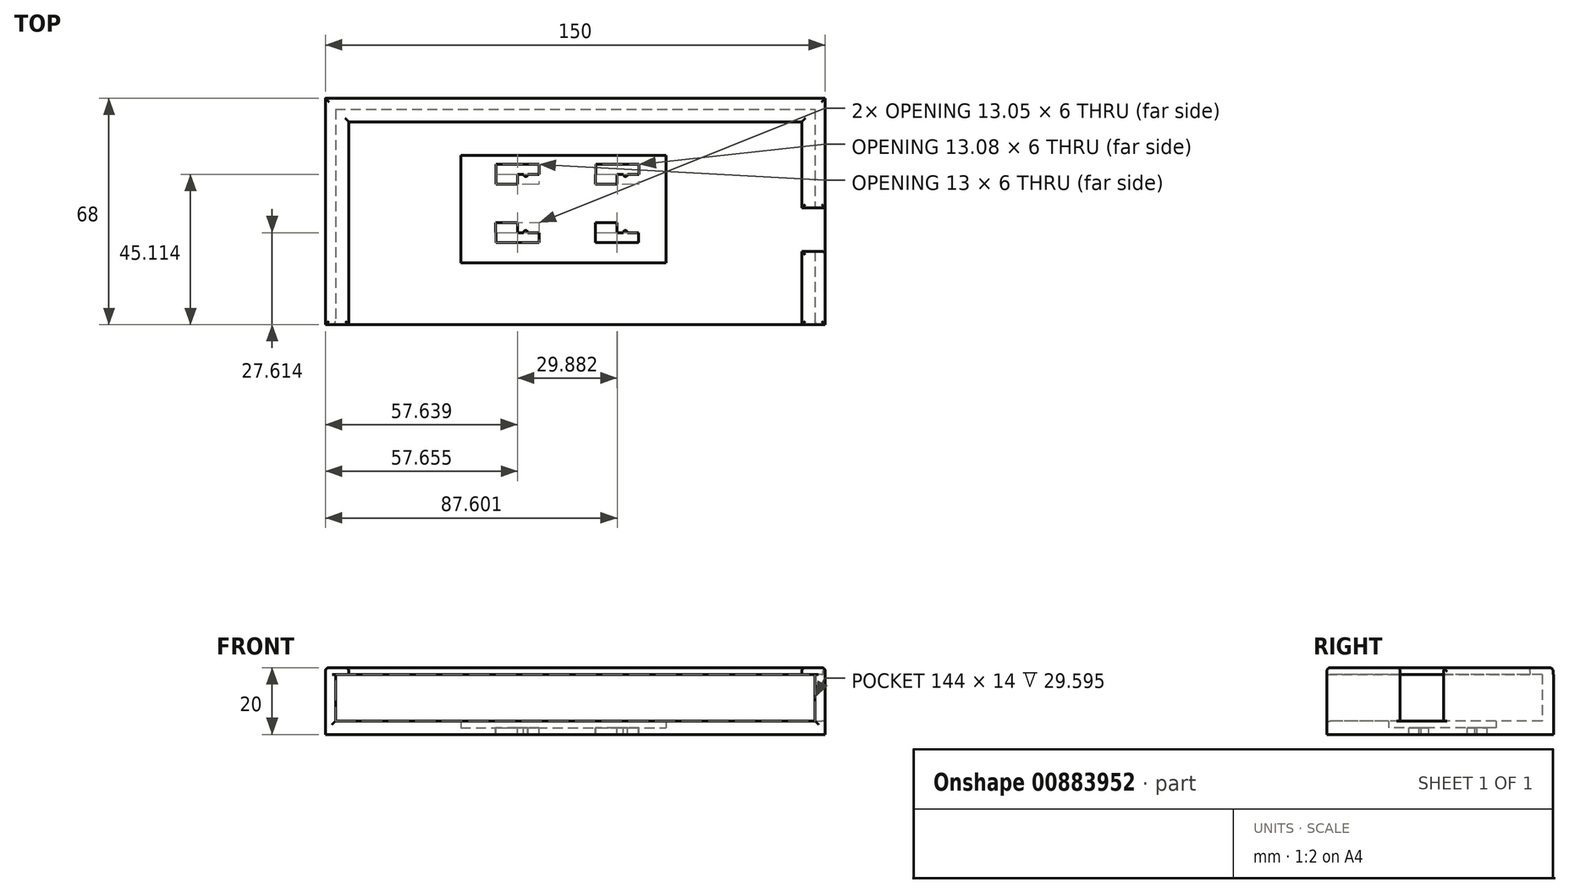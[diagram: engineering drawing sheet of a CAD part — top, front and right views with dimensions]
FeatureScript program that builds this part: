
annotation { "Feature Type Name" : "Feature", "Feature Type Description" : "" }
export const myFeature = defineFeature(function(context is Context, id is Id, definition is map)
    precondition{}
    {
        {
            var Q0;
            Q0=qCreatedBy(makeId("Top.planeOp"),FACE);
            var sketch = newSketch(context, id + "F0", { "sketchPlane" : qUnion([Q0])});
            skLineSegment(sketch, "E0", {"start": v(0, 0) * mm, "end": v(150, 0) * mm});
            skLineSegment(sketch, "E1", {"start": v(150, 0) * mm, "end": v(150, 68) * mm});
            skLineSegment(sketch, "E2", {"start": v(150, 68) * mm, "end": v(0, 68) * mm});
            skLineSegment(sketch, "E3", {"start": v(0, 68) * mm, "end": v(0, 0) * mm});
            skPoint(sketch, "E4.middle", {"position": v(71.45, 34.65) * mm});
            skLineSegment(sketch, "E5.bottom", {"start": v(40.6, 50.8) * mm, "end": v(102.3, 50.8) * mm});
            skLineSegment(sketch, "E5.top", {"start": v(40.6, 18.51) * mm, "end": v(102.3, 18.51) * mm});
            skLineSegment(sketch, "E5.left", {"start": v(40.6, 50.8) * mm, "end": v(40.6, 18.51) * mm});
            skLineSegment(sketch, "E5.right", {"start": v(102.3, 50.8) * mm, "end": v(102.3, 18.51) * mm});
            skSolve(sketch);
        }
        {
            var Q0;
            Q0=makeQuery(id+"F0.imprint","IMPRINT",FACE,{"disambiguationData":[TD([[makeQuery(id+"F0.imprint","IMPRINT",EDGE,{"derivedFrom":sQuery(id+"F0.wireOp",EDGE,"E0")}),1.0]])]});
            extrude(context, id + "F1", {"entities" : qUnion([Q0]), "depth" : 2 * mm, "offsetDistance" : 25.4 * mm});
        }
        {
            var Q0;
            Q0=makeQuery(id+"F1.opExtrude","CAP_FACE",FACE,{"disambiguationData":[OSD([sQuery(id+"F0.wireOp",EDGE,"E0"),sQuery(id+"F0.wireOp",EDGE,"E1"),sQuery(id+"F0.wireOp",EDGE,"E2"),sQuery(id+"F0.wireOp",EDGE,"E3")])],"isStart":false});
            var sketch = newSketch(context, id + "F2", { "sketchPlane" : qUnion([Q0])});
            skLineSegment(sketch, "E6.bottom", {"start": v(0, 68) * mm, "end": v(3, 68) * mm});
            skLineSegment(sketch, "E6.top", {"start": v(0, 0) * mm, "end": v(3, 0) * mm});
            skLineSegment(sketch, "E6.left", {"start": v(0, 68) * mm, "end": v(0, 0) * mm});
            skLineSegment(sketch, "E6.right", {"start": v(3, 68) * mm, "end": v(3, 0) * mm});
            skLineSegment(sketch, "E7.bottom", {"start": v(0, 68) * mm, "end": v(150, 68) * mm});
            skLineSegment(sketch, "E7.top", {"start": v(0, 64.6) * mm, "end": v(150, 64.6) * mm});
            skLineSegment(sketch, "E7.left", {"start": v(0, 68) * mm, "end": v(0, 64.6) * mm});
            skLineSegment(sketch, "E7.right", {"start": v(150, 68) * mm, "end": v(150, 64.6) * mm});
            skLineSegment(sketch, "E8.bottom", {"start": v(150, 68) * mm, "end": v(147, 68) * mm});
            skLineSegment(sketch, "E8.top", {"start": v(150, 35) * mm, "end": v(147, 35) * mm});
            skLineSegment(sketch, "E8.left", {"start": v(150, 68) * mm, "end": v(150, 35) * mm});
            skLineSegment(sketch, "E8.right", {"start": v(147, 68) * mm, "end": v(147, 35) * mm});
            skLineSegment(sketch, "E9.bottom", {"start": v(147, 22) * mm, "end": v(150, 22) * mm});
            skLineSegment(sketch, "E9.top", {"start": v(147, 0) * mm, "end": v(150, 0) * mm});
            skLineSegment(sketch, "E9.left", {"start": v(147, 22) * mm, "end": v(147, 0) * mm});
            skLineSegment(sketch, "E9.right", {"start": v(150, 22) * mm, "end": v(150, 0) * mm});
            skSolve(sketch);
        }
        {
            var Q0;
            Q0 = qSketchRegion(id + "F2", true);
            extrude(context, id + "F3", {"entities" : qUnion([Q0]), "operationType" : NewBodyOperationType.ADD, "depth" : 14 * mm, "offsetDistance" : 25 * mm});
        }
        {
            var Q0;
            Q0=makeQuery(id+"F3.opExtrude","CAP_FACE",FACE,{"disambiguationData":[OSD([sQuery(id+"F2.wireOp",EDGE,"E9.bottom"),sQuery(id+"F2.wireOp",EDGE,"E9.top"),sQuery(id+"F2.wireOp",EDGE,"E9.left"),sQuery(id+"F2.wireOp",EDGE,"E9.right")])],"isStart":false});
            var sketch = newSketch(context, id + "F4", { "sketchPlane" : qUnion([Q0])});
            skLineSegment(sketch, "E10.bottom", {"start": v(0, 0) * mm, "end": v(7, 0) * mm});
            skLineSegment(sketch, "E10.top", {"start": v(0, 67.89) * mm, "end": v(7, 67.89) * mm});
            skLineSegment(sketch, "E10.left", {"start": v(0, 0) * mm, "end": v(0, 67.89) * mm});
            skLineSegment(sketch, "E10.right", {"start": v(7, 0) * mm, "end": v(7, 67.89) * mm});
            skLineSegment(sketch, "E11.bottom", {"start": v(150, 67.89) * mm, "end": v(2.12, 67.89) * mm});
            skLineSegment(sketch, "E11.top", {"start": v(150, 60.89) * mm, "end": v(2.12, 60.89) * mm});
            skLineSegment(sketch, "E11.left", {"start": v(150, 67.89) * mm, "end": v(150, 60.89) * mm});
            skLineSegment(sketch, "E11.right", {"start": v(2.12, 67.89) * mm, "end": v(2.12, 60.89) * mm});
            skLineSegment(sketch, "E12.bottom", {"start": v(150, 67.89) * mm, "end": v(143, 67.89) * mm});
            skLineSegment(sketch, "E12.top", {"start": v(150, 35.06) * mm, "end": v(143, 35.06) * mm});
            skLineSegment(sketch, "E12.left", {"start": v(150, 67.89) * mm, "end": v(150, 35.06) * mm});
            skLineSegment(sketch, "E12.right", {"start": v(143, 67.89) * mm, "end": v(143, 35.06) * mm});
            skLineSegment(sketch, "E13.bottom", {"start": v(150, 22) * mm, "end": v(143, 22) * mm});
            skLineSegment(sketch, "E13.top", {"start": v(150, 0) * mm, "end": v(143, 0) * mm});
            skLineSegment(sketch, "E13.left", {"start": v(150, 22) * mm, "end": v(150, 0) * mm});
            skLineSegment(sketch, "E13.right", {"start": v(143, 22) * mm, "end": v(143, 0) * mm});
            skSolve(sketch);
        }
        {
            var Q0;
            Q0 = qSketchRegion(id + "F4", true);
            extrude(context, id + "F5", {"entities" : qUnion([Q0]), "operationType" : NewBodyOperationType.ADD, "depth" : 2 * mm, "offsetDistance" : 25 * mm});
        }
        {
            var Q0;
            Q0=makeQuery(id+"F5.opExtrude","CAP_FACE",FACE,{"disambiguationData":[OSD([sQuery(id+"FiIoThdrbuQYRGj_1.wireOp",EDGE,"L3UAmbnm-EkDf-mFo3-Kdad-xyRyGApwfJRc.bottom"),sQuery(id+"FiIoThdrbuQYRGj_1.wireOp",EDGE,"L3UAmbnm-EkDf-mFo3-Kdad-xyRyGApwfJRc.left"),sQuery(id+"FiIoThdrbuQYRGj_1.wireOp",EDGE,"L3UAmbnm-EkDf-mFo3-Kdad-xyRyGApwfJRc.right"),sQuery(id+"FiIoThdrbuQYRGj_1.wireOp",EDGE,"uIhgMk2j-Wb2O-wS5H-a29H-LI44CcTOFone.bottom"),sQuery(id+"FiIoThdrbuQYRGj_1.wireOp",EDGE,"uIhgMk2j-Wb2O-wS5H-a29H-LI44CcTOFone.top"),sQuery(id+"FiIoThdrbuQYRGj_1.wireOp",EDGE,"uIhgMk2j-Wb2O-wS5H-a29H-LI44CcTOFone.left"),sQuery(id+"FiIoThdrbuQYRGj_1.wireOp",EDGE,"GDGa2rMQ-mUk1-ouYS-nPaK-3d2uHhT5EnK0.bottom"),sQuery(id+"FiIoThdrbuQYRGj_1.wireOp",EDGE,"GDGa2rMQ-mUk1-ouYS-nPaK-3d2uHhT5EnK0.top"),sQuery(id+"FiIoThdrbuQYRGj_1.wireOp",EDGE,"GDGa2rMQ-mUk1-ouYS-nPaK-3d2uHhT5EnK0.left"),sQuery(id+"FiIoThdrbuQYRGj_1.wireOp",EDGE,"GDGa2rMQ-mUk1-ouYS-nPaK-3d2uHhT5EnK0.right")])],"isStart":false});
            var Q1;
            Q1=makeQuery(id+"F5.opExtrude","CAP_FACE",FACE,{"disambiguationData":[OSD([sQuery(id+"F4.wireOp",EDGE,"E10.bottom"),sQuery(id+"F4.wireOp",EDGE,"E10.top"),sQuery(id+"F4.wireOp",EDGE,"E10.left"),sQuery(id+"F4.wireOp",EDGE,"E10.right"),sQuery(id+"F4.wireOp",EDGE,"E11.bottom"),sQuery(id+"F4.wireOp",EDGE,"E11.top"),sQuery(id+"F4.wireOp",EDGE,"E12.bottom"),sQuery(id+"F4.wireOp",EDGE,"E12.top"),sQuery(id+"F4.wireOp",EDGE,"E12.left"),sQuery(id+"F4.wireOp",EDGE,"E12.right")])],"isStart":false});
            var Q2;
            Q2=makeQuery(id+"F5.opExtrude","CAP_FACE",FACE,{"disambiguationData":[OSD([sQuery(id+"F4.wireOp",EDGE,"E13.bottom"),sQuery(id+"F4.wireOp",EDGE,"E13.top"),sQuery(id+"F4.wireOp",EDGE,"E13.left"),sQuery(id+"F4.wireOp",EDGE,"E13.right")])],"isStart":false});
            var Q3;
            Q3=makeQuery(id+"F1.opExtrude","CAP_EDGE",EDGE,{"disambiguationData":[OSD([sQuery(id+"F0.wireOp",EDGE,"E0")])],"isStart":false});
            var Q4;
            Q4=makeQuery(id+"F3.opExtrude","SWEPT_EDGE",EDGE,{"disambiguationData":[OSD([sQuery(id+"F0.wireOp",EDGE,"E0"),sQuery(id+"F2.wireOp",EDGE,"E6.top"),sQuery(id+"F2.wireOp",EDGE,"E6.right")])]});
            var Q5;
            Q5=makeQuery(id+"F3.opExtrude","SWEPT_EDGE",EDGE,{"disambiguationData":[OSD([sQuery(id+"F0.wireOp",EDGE,"E0"),sQuery(id+"F2.wireOp",EDGE,"E9.top"),sQuery(id+"F2.wireOp",EDGE,"E9.left")])]});
            var Q6;
            Q6=makeQuery(id+"F5.boolean.opBoolean","MERGE",EDGE,{"derivedFrom":[makeQuery(id+"F3.opExtrude","SWEPT_EDGE",EDGE,{"disambiguationData":[OSD([sQuery(id+"F0.wireOp",EDGE,"E1"),sQuery(id+"F2.wireOp",EDGE,"E9.bottom"),sQuery(id+"F2.wireOp",EDGE,"E9.right")])]}),makeQuery(id+"F5.opExtrude","SWEPT_EDGE",EDGE,{"disambiguationData":[OSD([sQuery(id+"F4.wireOp",EDGE,"E13.bottom"),sQuery(id+"F4.wireOp",EDGE,"E13.left")])]})]});
            var Q7;
            Q7=makeQuery(id+"F3.opExtrude","SWEPT_EDGE",EDGE,{"disambiguationData":[OSD([sQuery(id+"F0.wireOp",EDGE,"E1"),sQuery(id+"F2.wireOp",EDGE,"E8.top"),sQuery(id+"F2.wireOp",EDGE,"E8.left")])]});
            fillet(context, id + "F6", {"entities" : qUnion([Q0, Q1, Q2, Q3, Q4, Q5, Q6, Q7]), "radius" : 1 * mm, "tangentPropagation" : true, "allowEdgeOverflow" : false});
        }
        {
            var Q0;
            Q0=makeQuery(id+"F0.imprint","IMPRINT",FACE,{"disambiguationData":[TD([[makeQuery(id+"F0.imprint","IMPRINT",EDGE,{"derivedFrom":sQuery(id+"F0.wireOp",EDGE,"E0")}),1.0]])]});
            var sketch = newSketch(context, id + "F7", { "sketchPlane" : qUnion([Q0])});
            skSolve(sketch);
        }
        {
            var Q0;
            Q0=makeQuery(id+"F7.imprint","IMPRINT",FACE,{"disambiguationData":[TD([[makeQuery(id+"F7.imprint","IMPRINT",EDGE,{"derivedFrom":makeQuery(id+"F0.imprint","IMPRINT",EDGE,{"derivedFrom":sQuery(id+"F0.wireOp",EDGE,"E0")})}),1.0]])]});
            extrude(context, id + "F8", {"entities" : qUnion([Q0]), "operationType" : NewBodyOperationType.ADD, "oppositeDirection" : true, "depth" : 2 * mm, "offsetDistance" : 25 * mm});
        }
        {
            var Q0;
            Q0=makeQuery(id+"F0.imprint","IMPRINT",FACE,{"disambiguationData":[TD([[makeQuery(id+"F0.imprint","IMPRINT",EDGE,{"derivedFrom":sQuery(id+"F0.wireOp",EDGE,"E0")}),1.0]])]});
            var sketch = newSketch(context, id + "F9", { "sketchPlane" : qUnion([Q0])});
            skLineSegment(sketch, "E14.bottom", {"start": v(35.79, 54.11) * mm, "end": v(109.69, 54.11) * mm});
            skLineSegment(sketch, "E14.top", {"start": v(35.79, 15.02) * mm, "end": v(109.69, 15.02) * mm});
            skLineSegment(sketch, "E14.left", {"start": v(35.79, 54.11) * mm, "end": v(35.79, 15.02) * mm});
            skLineSegment(sketch, "E14.right", {"start": v(109.69, 54.11) * mm, "end": v(109.69, 15.02) * mm});
            skPoint(sketch, "E14.middle", {"position": v(72.74, 34.57) * mm});
            skLineSegment(sketch, "E15", {"start": v(51.14, 48.11) * mm, "end": v(64.14, 48.11) * mm});
            skLineSegment(sketch, "E16", {"start": v(64.14, 48.11) * mm, "end": v(64.14, 45.11) * mm});
            skLineSegment(sketch, "E17", {"start": v(64.14, 45.11) * mm, "end": v(57.64, 45.11) * mm});
            skLineSegment(sketch, "E18", {"start": v(57.64, 45.11) * mm, "end": v(57.64, 42.11) * mm});
            skLineSegment(sketch, "E19", {"start": v(51.14, 42.11) * mm, "end": v(51.14, 48.11) * mm});
            skLineSegment(sketch, "E20", {"start": v(81.14, 48.11) * mm, "end": v(94.14, 48.11) * mm});
            skLineSegment(sketch, "E21", {"start": v(94.14, 48.11) * mm, "end": v(94.14, 45.11) * mm});
            skLineSegment(sketch, "E22", {"start": v(94.14, 45.11) * mm, "end": v(87.56, 45.11) * mm});
            skLineSegment(sketch, "E23", {"start": v(87.56, 45.11) * mm, "end": v(87.56, 42.11) * mm});
            skLineSegment(sketch, "E24", {"start": v(87.56, 42.11) * mm, "end": v(81.06, 42.11) * mm});
            skLineSegment(sketch, "E25", {"start": v(81.06, 42.11) * mm, "end": v(81.14, 48.11) * mm});
            skLineSegment(sketch, "E26", {"start": v(51.14, 42.11) * mm, "end": v(57.64, 42.11) * mm});
            skLineSegment(sketch, "E27", {"start": v(51.18, 24.61) * mm, "end": v(64.18, 24.61) * mm});
            skLineSegment(sketch, "E28", {"start": v(64.18, 24.61) * mm, "end": v(64.18, 27.61) * mm});
            skLineSegment(sketch, "E29", {"start": v(64.18, 27.61) * mm, "end": v(57.63, 27.61) * mm});
            skLineSegment(sketch, "E30", {"start": v(57.63, 27.61) * mm, "end": v(57.63, 30.61) * mm});
            skLineSegment(sketch, "E31", {"start": v(57.63, 30.61) * mm, "end": v(51.13, 30.61) * mm});
            skLineSegment(sketch, "E32", {"start": v(51.13, 30.61) * mm, "end": v(51.18, 24.61) * mm});
            skLineSegment(sketch, "E33", {"start": v(81.06, 24.61) * mm, "end": v(94.06, 24.61) * mm});
            skLineSegment(sketch, "E34", {"start": v(94.06, 24.61) * mm, "end": v(94.06, 27.61) * mm});
            skLineSegment(sketch, "E35", {"start": v(94.06, 27.61) * mm, "end": v(87.51, 27.61) * mm});
            skLineSegment(sketch, "E36", {"start": v(87.51, 27.61) * mm, "end": v(87.51, 30.61) * mm});
            skLineSegment(sketch, "E37", {"start": v(87.51, 30.61) * mm, "end": v(81.01, 30.61) * mm});
            skLineSegment(sketch, "E38", {"start": v(81.01, 30.61) * mm, "end": v(81.06, 24.61) * mm});
            skCircle(sketch, "E39", {"center": v(60.14, 45.11) * mm, "radius": 0.65 * mm});
            skCircle(sketch, "E40", {"center": v(90.06, 45.11) * mm, "radius": 0.65 * mm});
            skCircle(sketch, "E41", {"center": v(90.01, 27.61) * mm, "radius": 0.65 * mm});
            skCircle(sketch, "E42", {"center": v(60.13, 27.61) * mm, "radius": 0.65 * mm});
            skSolve(sketch);
        }
        {
            var Q0;
            Q0=makeQuery(id+"F9.imprint","IMPRINT",FACE,{"disambiguationData":[TD([[makeQuery(id+"F9.imprint","IMPRINT",EDGE,{"derivedFrom":sQuery(id+"F9.wireOp",EDGE,"E14.bottom")}),-1.0]])]});
            var Q1;
            Q1=makeQuery(id+"F9.imprint","IMPRINT",FACE,{"disambiguationData":[TD([[makeQuery(id+"F9.imprint","IMPRINT",EDGE,{"derivedFrom":sQuery(id+"F9.wireOp",EDGE,"E15")}),1.0]])]});
            extrude(context, id + "F10", {"entities" : qUnion([Q0, Q1]), "operationType" : NewBodyOperationType.ADD, "oppositeDirection" : true, "depth" : 2 * mm, "offsetDistance" : 25 * mm});
        }
    });
